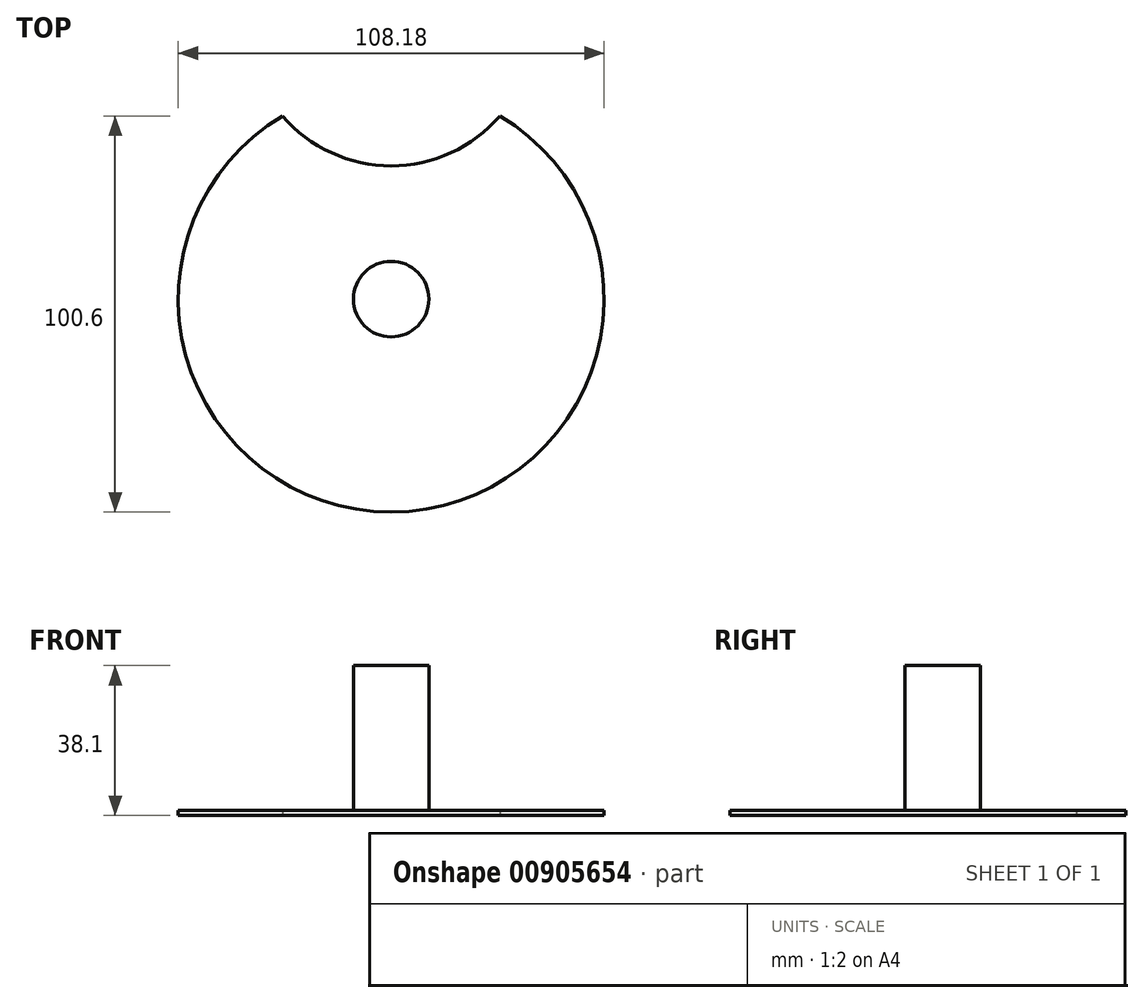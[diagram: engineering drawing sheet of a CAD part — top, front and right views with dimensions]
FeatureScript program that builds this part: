
annotation { "Feature Type Name" : "Feature", "Feature Type Description" : "" }
export const myFeature = defineFeature(function(context is Context, id is Id, definition is map)
    precondition{}
    {
        {
            var Q0;
            Q0=qCreatedBy(makeId("Top.planeOp"),FACE);
            var sketch = newSketch(context, id + "F0", { "sketchPlane" : qUnion([Q0])});
            skCircle(sketch, "E0", {"center": v(0, 0) * mm, "radius": 54.1 * mm});
            skSolve(sketch);
        }
        {
            var Q0;
            Q0=makeQuery(id+"F0.imprint","IMPRINT",FACE,{"disambiguationData":[TD([[makeQuery(id+"F0.imprint","IMPRINT",EDGE,{"derivedFrom":sQuery(id+"F0.wireOp",EDGE,"E0")}),1.0]])]});
            extrude(context, id + "F1", {"entities" : qUnion([Q0]), "depth" : 1.27 * mm, "offsetDistance" : 25.4 * mm});
        }
        {
            var Q0;
            Q0=qCreatedBy(makeId("Top.planeOp"),FACE);
            var sketch = newSketch(context, id + "F2", { "sketchPlane" : qUnion([Q0])});
            skCircle(sketch, "E1", {"center": v(0, 70.34) * mm, "radius": 36.48 * mm});
            skSolve(sketch);
        }
        {
            var Q0;
            Q0=makeQuery(id+"F2.imprint","IMPRINT",FACE,{"disambiguationData":[TD([[makeQuery(id+"F2.imprint","IMPRINT",EDGE,{"derivedFrom":sQuery(id+"F2.wireOp",EDGE,"E1")}),1.0]])]});
            extrude(context, id + "F3", {"entities" : qUnion([Q0]), "operationType" : NewBodyOperationType.REMOVE, "depth" : 25.4 * mm, "offsetDistance" : 25.4 * mm});
        }
        {
            var Q0;
            Q0=qCreatedBy(makeId("Top.planeOp"),FACE);
            var sketch = newSketch(context, id + "F4", { "sketchPlane" : qUnion([Q0])});
            skCircle(sketch, "E2", {"center": v(0, 0) * mm, "radius": 9.6 * mm});
            skSolve(sketch);
        }
        {
            var Q0;
            Q0=makeQuery(id+"F4.imprint","IMPRINT",FACE,{"disambiguationData":[TD([[makeQuery(id+"F4.imprint","IMPRINT",EDGE,{"derivedFrom":sQuery(id+"F4.wireOp",EDGE,"E2")}),1.0]])]});
            var Q1;
            Q1=sQuery(id+"F4.wireOp",EDGE,"E2");
            extrude(context, id + "F5", {"entities" : qUnion([Q0]), "operationType" : NewBodyOperationType.ADD, "surfaceEntities" : qUnion([Q1]), "depth" : 38.1 * mm, "offsetDistance" : 25.4 * mm});
        }
        {
            var Q0;
            Q0=qCreatedBy(makeId("Top.planeOp"),FACE);
            var sketch = newSketch(context, id + "F6", { "sketchPlane" : qUnion([Q0])});
            skLineSegment(sketch, "E3.bottom", {"start": v(-5.25, 13.35) * mm, "end": v(5.25, 13.35) * mm});
            skLineSegment(sketch, "E3.top", {"start": v(-5.25, 27.15) * mm, "end": v(5.25, 27.15) * mm});
            skLineSegment(sketch, "E3.left", {"start": v(-5.25, 13.35) * mm, "end": v(-5.25, 27.15) * mm});
            skLineSegment(sketch, "E3.right", {"start": v(5.25, 13.35) * mm, "end": v(5.25, 27.15) * mm});
            skPoint(sketch, "E3.middle", {"position": v(0, 20.25) * mm});
            skSolve(sketch);
        }
        {
            var Q0;
            Q0=sQuery(id+"F6.wireOp",EDGE,"E3.left");
            var Q1;
            Q1=sQuery(id+"F6.wireOp",EDGE,"E3.bottom");
            var Q2;
            Q2=sQuery(id+"F6.wireOp",EDGE,"E3.top");
            var Q3;
            Q3=sQuery(id+"F6.wireOp",EDGE,"E3.right");
            extrude(context, id + "F7", {"bodyType" : ToolBodyType.SURFACE, "surfaceEntities" : qUnion([Q0, Q1, Q2, Q3]), "depth" : 50.8 * mm, "offsetDistance" : 25.4 * mm});
        }
        {
            var Q0;
            Q0=qCreatedBy(makeId("Right.planeOp"),FACE);
            var sketch = newSketch(context, id + "F8", { "sketchPlane" : qUnion([Q0])});
            skLineSegment(sketch, "E4.bottom", {"start": v(27.13, 42.8) * mm, "end": v(13.37, 42.8) * mm});
            skLineSegment(sketch, "E4.top", {"start": v(27.13, 50.78) * mm, "end": v(13.37, 50.78) * mm});
            skLineSegment(sketch, "E4.left", {"start": v(27.13, 42.8) * mm, "end": v(27.13, 50.78) * mm});
            skLineSegment(sketch, "E4.right", {"start": v(13.37, 42.8) * mm, "end": v(13.37, 50.78) * mm});
            skSolve(sketch);
        }
        {
            var Q0;
            Q0=sQuery(id+"F8.wireOp",EDGE,"E4.right");
            var Q1;
            Q1=sQuery(id+"F8.wireOp",EDGE,"E4.bottom");
            var Q2;
            Q2=sQuery(id+"F8.wireOp",EDGE,"E4.left");
            var Q3;
            Q3=sQuery(id+"F8.wireOp",EDGE,"E4.top");
            extrude(context, id + "F9", {"bodyType" : ToolBodyType.SURFACE, "surfaceEntities" : qUnion([Q0, Q1, Q2, Q3]), "depth" : 25.4 * mm, "offsetDistance" : 25.4 * mm});
        }
    });
